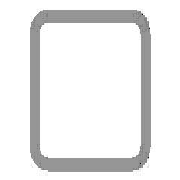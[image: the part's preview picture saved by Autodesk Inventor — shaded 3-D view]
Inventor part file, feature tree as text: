
AUTODESK INVENTOR PART (.ipt)
format: ipt  version: 2025 (Build 290162010, 162A)  size: 133,120 bytes
history: native  units: mm (DEFAULTED — no unit token found)
features: other x4, sketch x1, plane x1
ambient origin geometry x8: Origin, YZ Plane, XZ Plane, XY Plane, X Axis, Y Axis, Z Axis, Center Point
bodies: Solid1 (feature_tree), Body (feature_tree)
feature tree (6):
  parser-record x1  (decoder bookkeeping rows leaked as tree rows — omitted from the tree; the rows remain in map.json)
  other  "Driven Length"
  other  "Start Plane"
  other  "End Plane"
  sketch  "Sketch3"  dims[d3=790.0mm d4=0.0mm d7=4.0mm d9=40.0mm d11=40.0mm d12=2.0mm d13=-0.0mm d14=790.0mm d15=20.0mm d16=20.0mm d17=90.0deg d18=790.0mm]
  plane  "Work Plane3"
